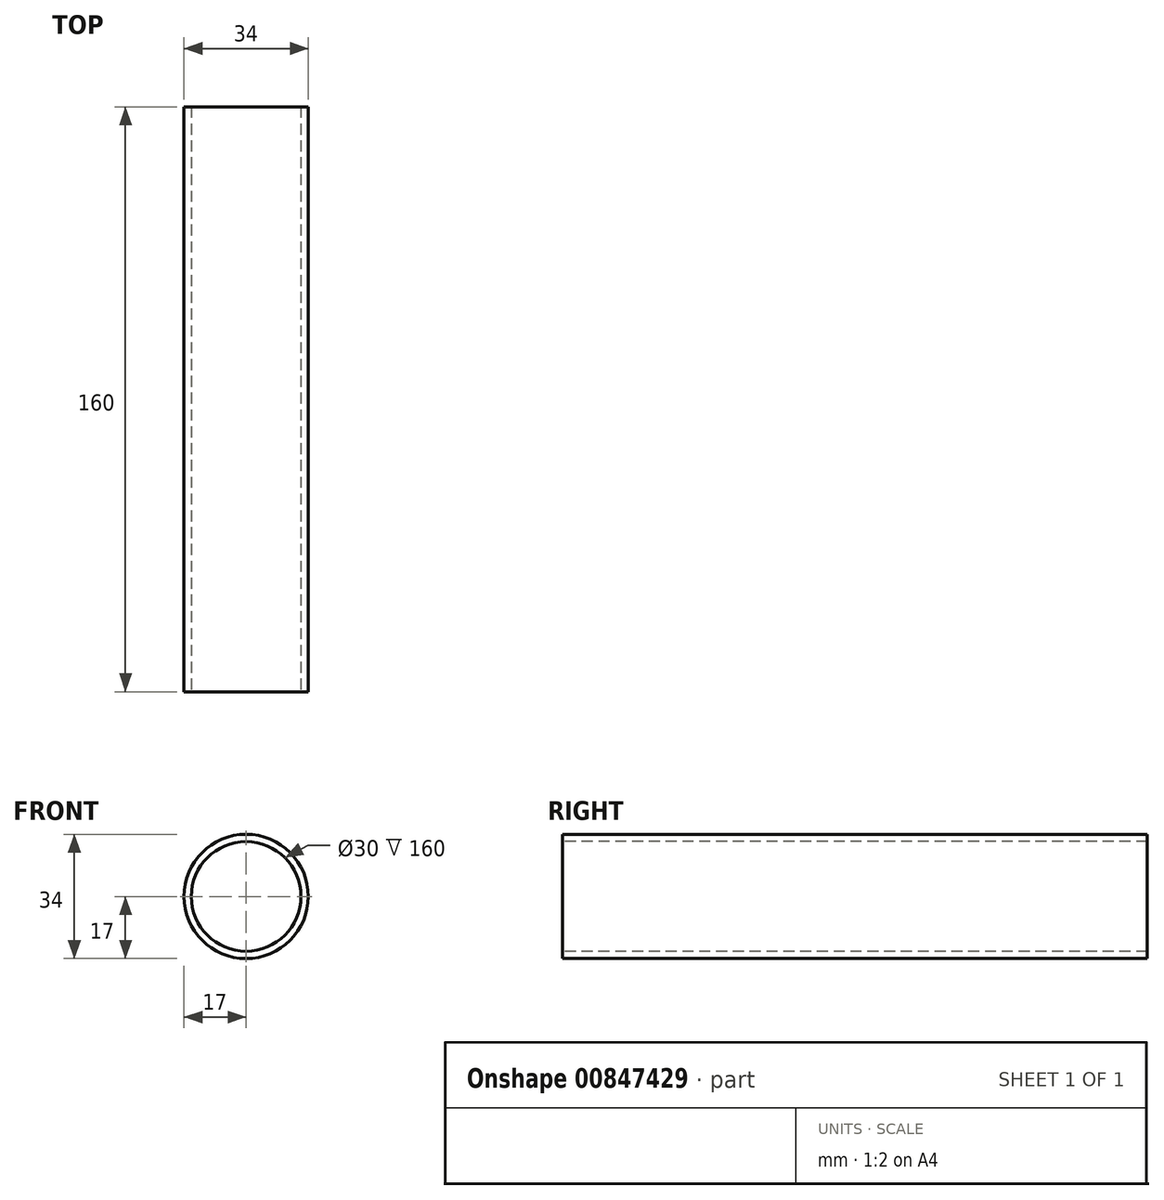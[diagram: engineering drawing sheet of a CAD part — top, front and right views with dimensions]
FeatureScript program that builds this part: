
annotation { "Feature Type Name" : "Feature", "Feature Type Description" : "" }
export const myFeature = defineFeature(function(context is Context, id is Id, definition is map)
    precondition{}
    {
        {
            var Q0;
            Q0=qCreatedBy(makeId("Front.planeOp"),FACE);
            var sketch = newSketch(context, id + "F0", { "sketchPlane" : qUnion([Q0])});
            skLineSegment(sketch, "E0", {"start": v(0, 40.58) * mm, "end": v(0, -41.33) * mm, "construction": true});
            skLineSegment(sketch, "E1", {"start": v(-47.51, 0) * mm, "end": v(52.14, 0) * mm, "construction": true});
            skCircle(sketch, "E2", {"center": v(0, 0) * mm, "radius": 17 * mm});
            skCircle(sketch, "E3.0", {"center": v(0, 0) * mm, "radius": 15 * mm});
            skSolve(sketch);
        }
        {
            var Q0;
            Q0 = qSketchRegion(id + "F0", true);
            extrude(context, id + "F1", {"entities" : qUnion([Q0]), "oppositeDirection" : true, "depth" : 160 * mm, "offsetDistance" : 25 * mm});
        }
    });
